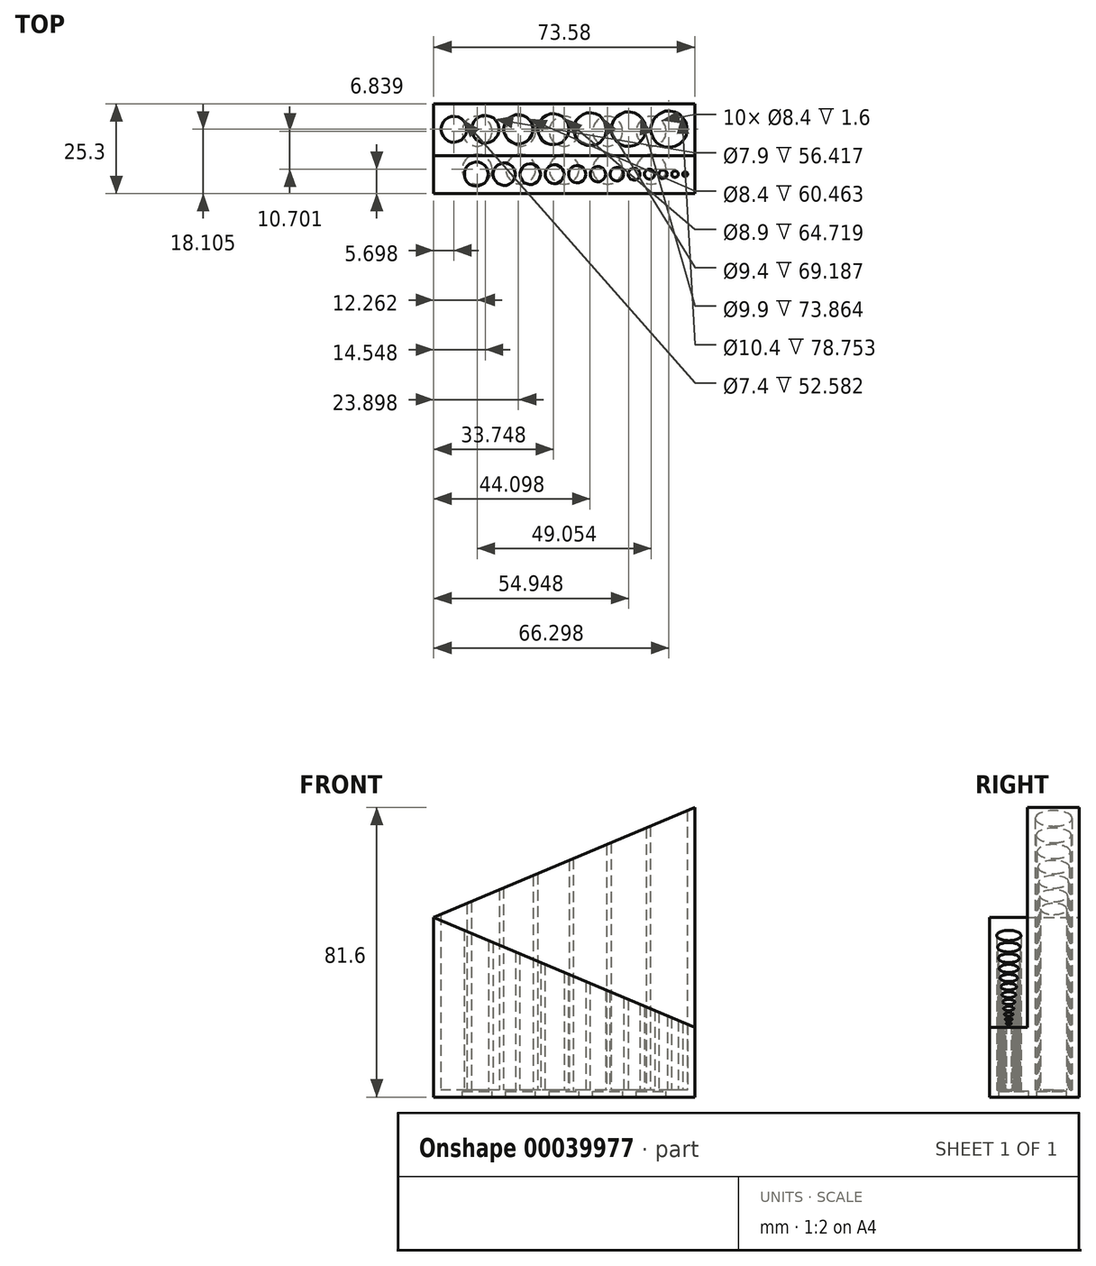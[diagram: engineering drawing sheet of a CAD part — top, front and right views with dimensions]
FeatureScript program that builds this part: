
annotation { "Feature Type Name" : "Feature", "Feature Type Description" : "" }
export const myFeature = defineFeature(function(context is Context, id is Id, definition is map)
    precondition{}
    {
        {
            var Q0;
            Q0=qCreatedBy(makeId("Top.planeOp"),FACE);
            var sketch = newSketch(context, id + "F0", { "sketchPlane" : qUnion([Q0])});
            skLineSegment(sketch, "E0.bottom", {"start": v(-27.23, 22.36) * mm, "end": v(46.35, 22.36) * mm});
            skLineSegment(sketch, "E0.top", {"start": v(-27.23, -2.94) * mm, "end": v(46.35, -2.94) * mm});
            skLineSegment(sketch, "E0.left", {"start": v(-27.23, 22.36) * mm, "end": v(-27.23, -2.94) * mm});
            skLineSegment(sketch, "E0.right", {"start": v(46.35, 22.36) * mm, "end": v(46.35, -2.94) * mm});
            skLineSegment(sketch, "E1", {"start": v(-27.23, 2.51) * mm, "end": v(46.35, 2.51) * mm, "construction": true});
            skCircle(sketch, "E2", {"center": v(43.65, 2.51) * mm, "radius": 0.7 * mm});
            skCircle(sketch, "E3", {"center": v(40.8, 2.51) * mm, "radius": 0.95 * mm});
            skCircle(sketch, "E4", {"center": v(37.45, 2.51) * mm, "radius": 1.2 * mm});
            skCircle(sketch, "E5", {"center": v(33.6, 2.51) * mm, "radius": 1.45 * mm});
            skCircle(sketch, "E6", {"center": v(29.25, 2.51) * mm, "radius": 1.7 * mm});
            skCircle(sketch, "E7", {"center": v(24.4, 2.51) * mm, "radius": 1.95 * mm});
            skCircle(sketch, "E8", {"center": v(19.05, 2.51) * mm, "radius": 2.2 * mm});
            skCircle(sketch, "E9", {"center": v(13.2, 2.51) * mm, "radius": 2.45 * mm});
            skLineSegment(sketch, "E10", {"start": v(-27.23, 15.16) * mm, "end": v(46.35, 15.16) * mm, "construction": true});
            skCircle(sketch, "E11", {"center": v(-12.68, 15.16) * mm, "radius": 3.95 * mm});
            skCircle(sketch, "E12", {"center": v(-3.33, 15.16) * mm, "radius": 4.2 * mm});
            skCircle(sketch, "E13", {"center": v(6.52, 15.16) * mm, "radius": 4.45 * mm});
            skCircle(sketch, "E14", {"center": v(16.87, 15.16) * mm, "radius": 4.7 * mm});
            skCircle(sketch, "E15", {"center": v(27.72, 15.16) * mm, "radius": 4.95 * mm});
            skCircle(sketch, "E16", {"center": v(39.07, 15.16) * mm, "radius": 5.2 * mm});
            skCircle(sketch, "E17", {"center": v(6.85, 2.51) * mm, "radius": 2.7 * mm});
            skCircle(sketch, "E18", {"center": v(0, 2.51) * mm, "radius": 2.95 * mm});
            skCircle(sketch, "E19", {"center": v(-7.35, 2.51) * mm, "radius": 3.2 * mm});
            skCircle(sketch, "E20", {"center": v(-21.53, 15.16) * mm, "radius": 3.7 * mm});
            skCircle(sketch, "E21", {"center": v(-15.2, 2.51) * mm, "radius": 3.45 * mm});
            skLineSegment(sketch, "E22", {"start": v(-27.23, 5.96) * mm, "end": v(46.35, 5.96) * mm, "construction": true});
            skLineSegment(sketch, "E23", {"start": v(-27.23, 9.96) * mm, "end": v(46.35, 9.96) * mm, "construction": true});
            skSolve(sketch);
        }
        {
            var Q0;
            Q0=makeQuery(id+"F0.imprint","IMPRINT",FACE,{"disambiguationData":[TD([[makeQuery(id+"F0.imprint","IMPRINT",EDGE,{"derivedFrom":sQuery(id+"F0.wireOp",EDGE,"E0.bottom")}),-1.0]])]});
            extrude(context, id + "F1", {"entities" : qUnion([Q0]), "depth" : 80 * mm});
        }
        {
            var Q0;
            Q0=makeQuery(id+"F1.opExtrude","SWEPT_FACE",FACE,{"disambiguationData":[OSD([sQuery(id+"F0.wireOp",EDGE,"E0.top")])]});
            var sketch = newSketch(context, id + "F2", { "sketchPlane" : qUnion([Q0])});
            skLineSegment(sketch, "E24", {"start": v(-27.23, 0) * mm, "end": v(46.35, 0) * mm});
            skLineSegment(sketch, "E25", {"start": v(46.35, 0) * mm, "end": v(46.35, 18) * mm});
            skLineSegment(sketch, "E26", {"start": v(46.35, 18) * mm, "end": v(-27.23, 49) * mm});
            skLineSegment(sketch, "E27", {"start": v(-27.23, 49) * mm, "end": v(-27.23, 0) * mm});
            skSolve(sketch);
        }
        {
            var Q0;
            Q0=makeQuery(id+"F0.imprint","IMPRINT",FACE,{"disambiguationData":[TD([[makeQuery(id+"F0.imprint","IMPRINT",EDGE,{"derivedFrom":sQuery(id+"F0.wireOp",EDGE,"E16")}),1.0]])]});
            var Q1;
            Q1=makeQuery(id+"F0.imprint","IMPRINT",FACE,{"disambiguationData":[TD([[makeQuery(id+"F0.imprint","IMPRINT",EDGE,{"derivedFrom":sQuery(id+"F0.wireOp",EDGE,"E15")}),1.0]])]});
            var Q2;
            Q2=makeQuery(id+"F0.imprint","IMPRINT",FACE,{"disambiguationData":[TD([[makeQuery(id+"F0.imprint","IMPRINT",EDGE,{"derivedFrom":sQuery(id+"F0.wireOp",EDGE,"E14")}),1.0]])]});
            var Q3;
            Q3=makeQuery(id+"F0.imprint","IMPRINT",FACE,{"disambiguationData":[TD([[makeQuery(id+"F0.imprint","IMPRINT",EDGE,{"derivedFrom":sQuery(id+"F0.wireOp",EDGE,"E13")}),1.0]])]});
            var Q4;
            Q4=makeQuery(id+"F0.imprint","IMPRINT",FACE,{"disambiguationData":[TD([[makeQuery(id+"F0.imprint","IMPRINT",EDGE,{"derivedFrom":sQuery(id+"F0.wireOp",EDGE,"E12")}),1.0]])]});
            var Q5;
            Q5=makeQuery(id+"F0.imprint","IMPRINT",FACE,{"disambiguationData":[TD([[makeQuery(id+"F0.imprint","IMPRINT",EDGE,{"derivedFrom":sQuery(id+"F0.wireOp",EDGE,"E11")}),1.0]])]});
            var Q6;
            Q6=makeQuery(id+"F0.imprint","IMPRINT",FACE,{"disambiguationData":[TD([[makeQuery(id+"F0.imprint","IMPRINT",EDGE,{"derivedFrom":sQuery(id+"F0.wireOp",EDGE,"E20")}),1.0]])]});
            var Q7;
            Q7=makeQuery(id+"F0.imprint","IMPRINT",FACE,{"disambiguationData":[TD([[makeQuery(id+"F0.imprint","IMPRINT",EDGE,{"derivedFrom":sQuery(id+"F0.wireOp",EDGE,"E19")}),1.0]])]});
            var Q8;
            Q8=makeQuery(id+"F0.imprint","IMPRINT",FACE,{"disambiguationData":[TD([[makeQuery(id+"F0.imprint","IMPRINT",EDGE,{"derivedFrom":sQuery(id+"F0.wireOp",EDGE,"E18")}),1.0]])]});
            var Q9;
            Q9=makeQuery(id+"F0.imprint","IMPRINT",FACE,{"disambiguationData":[TD([[makeQuery(id+"F0.imprint","IMPRINT",EDGE,{"derivedFrom":sQuery(id+"F0.wireOp",EDGE,"E17")}),1.0]])]});
            var Q10;
            Q10=makeQuery(id+"F0.imprint","IMPRINT",FACE,{"disambiguationData":[TD([[makeQuery(id+"F0.imprint","IMPRINT",EDGE,{"derivedFrom":sQuery(id+"F0.wireOp",EDGE,"E9")}),1.0]])]});
            var Q11;
            Q11=makeQuery(id+"F0.imprint","IMPRINT",FACE,{"disambiguationData":[TD([[makeQuery(id+"F0.imprint","IMPRINT",EDGE,{"derivedFrom":sQuery(id+"F0.wireOp",EDGE,"E8")}),1.0]])]});
            var Q12;
            Q12=makeQuery(id+"F0.imprint","IMPRINT",FACE,{"disambiguationData":[TD([[makeQuery(id+"F0.imprint","IMPRINT",EDGE,{"derivedFrom":sQuery(id+"F0.wireOp",EDGE,"E7")}),1.0]])]});
            var Q13;
            Q13=makeQuery(id+"F0.imprint","IMPRINT",FACE,{"disambiguationData":[TD([[makeQuery(id+"F0.imprint","IMPRINT",EDGE,{"derivedFrom":sQuery(id+"F0.wireOp",EDGE,"E21")}),1.0]])]});
            var Q14;
            Q14=makeQuery(id+"F0.imprint","IMPRINT",FACE,{"disambiguationData":[TD([[makeQuery(id+"F0.imprint","IMPRINT",EDGE,{"derivedFrom":sQuery(id+"F0.wireOp",EDGE,"E6")}),1.0]])]});
            var Q15;
            Q15=makeQuery(id+"F0.imprint","IMPRINT",FACE,{"disambiguationData":[TD([[makeQuery(id+"F0.imprint","IMPRINT",EDGE,{"derivedFrom":sQuery(id+"F0.wireOp",EDGE,"E5")}),1.0]])]});
            var Q16;
            Q16=makeQuery(id+"F0.imprint","IMPRINT",FACE,{"disambiguationData":[TD([[makeQuery(id+"F0.imprint","IMPRINT",EDGE,{"derivedFrom":sQuery(id+"F0.wireOp",EDGE,"E4")}),1.0]])]});
            var Q17;
            Q17=makeQuery(id+"F0.imprint","IMPRINT",FACE,{"disambiguationData":[TD([[makeQuery(id+"F0.imprint","IMPRINT",EDGE,{"derivedFrom":sQuery(id+"F0.wireOp",EDGE,"E3")}),1.0]])]});
            var Q18;
            Q18=makeQuery(id+"F0.imprint","IMPRINT",FACE,{"disambiguationData":[TD([[makeQuery(id+"F0.imprint","IMPRINT",EDGE,{"derivedFrom":sQuery(id+"F0.wireOp",EDGE,"E0.bottom")}),-1.0]])]});
            var Q19;
            Q19=makeQuery(id+"F0.imprint","IMPRINT",FACE,{"disambiguationData":[TD([[makeQuery(id+"F0.imprint","IMPRINT",EDGE,{"derivedFrom":sQuery(id+"F0.wireOp",EDGE,"E2")}),1.0]])]});
            extrude(context, id + "F3", {"entities" : qUnion([Q0, Q1, Q2, Q3, Q4, Q5, Q6, Q7, Q8, Q9, Q10, Q11, Q12, Q13, Q14, Q15, Q16, Q17, Q18, Q19]), "depth" : 0.4 * mm});
        }
        {
            var Q0;
            {var subQ3=sQuery(id+"F2.wireOp",EDGE,"E26");Q0=makeQuery(id+"F2.imprint","IMPRINT",FACE,{"disambiguationData":[TD([[makeQuery(id+"F2.imprint","IMPRINT",EDGE,{"derivedFrom":subQ3}),-1.0]])]});}
            extrude(context, id + "F4", {"entities" : qUnion([Q0]), "operationType" : NewBodyOperationType.REMOVE, "oppositeDirection" : true, "depth" : 10.7 * mm});
        }
        {
            var Q0;
            Q0=makeQuery(id+"F1.opExtrude","SWEPT_FACE",FACE,{"disambiguationData":[OSD([sQuery(id+"F0.wireOp",EDGE,"E0.bottom")])]});
            var sketch = newSketch(context, id + "F5", { "sketchPlane" : qUnion([Q0])});
            skLineSegment(sketch, "E28", {"start": v(27.23, 0) * mm, "end": v(-46.35, 0) * mm});
            skLineSegment(sketch, "E29", {"start": v(-46.35, 0) * mm, "end": v(-46.35, 80) * mm});
            skLineSegment(sketch, "E30", {"start": v(-46.35, 80) * mm, "end": v(27.23, 49) * mm});
            skLineSegment(sketch, "E31", {"start": v(27.23, 49) * mm, "end": v(27.23, 0) * mm});
            skSolve(sketch);
        }
        {
            var Q0;
            {var subQ3=sQuery(id+"F5.wireOp",EDGE,"E30");Q0=makeQuery(id+"F5.imprint","IMPRINT",FACE,{"disambiguationData":[TD([[makeQuery(id+"F5.imprint","IMPRINT",EDGE,{"derivedFrom":subQ3}),1.0]])]});}
            extrude(context, id + "F6", {"entities" : qUnion([Q0]), "operationType" : NewBodyOperationType.REMOVE, "oppositeDirection" : true, "depth" : 25 * mm});
        }
        {
            var Q0;
            Q0=makeQuery(id+"F3.opExtrude","CAP_FACE",FACE,{"disambiguationData":[OSD([sQuery(id+"F0.wireOp",EDGE,"E0.bottom"),sQuery(id+"F0.wireOp",EDGE,"E0.top"),sQuery(id+"F0.wireOp",EDGE,"E0.left"),sQuery(id+"F0.wireOp",EDGE,"E0.right")])],"isStart":true});
            var sketch = newSketch(context, id + "F7", { "sketchPlane" : qUnion([Q0])});
            skLineSegment(sketch, "E32.bottom", {"start": v(-27.23, 2.94) * mm, "end": v(46.35, 2.94) * mm});
            skLineSegment(sketch, "E32.top", {"start": v(-27.23, -22.36) * mm, "end": v(46.35, -22.36) * mm});
            skLineSegment(sketch, "E32.left", {"start": v(-27.23, 2.94) * mm, "end": v(-27.23, -22.36) * mm});
            skLineSegment(sketch, "E32.right", {"start": v(46.35, 2.94) * mm, "end": v(46.35, -22.36) * mm});
            skCircle(sketch, "E33", {"center": v(-14.97, -3.9) * mm, "radius": 4.2 * mm});
            skCircle(sketch, "E34", {"center": v(-2.7, -3.9) * mm, "radius": 4.2 * mm});
            skCircle(sketch, "E35", {"center": v(9.56, -3.9) * mm, "radius": 4.2 * mm});
            skCircle(sketch, "E36", {"center": v(21.82, -3.9) * mm, "radius": 4.2 * mm});
            skCircle(sketch, "E37", {"center": v(34.09, -14.6) * mm, "radius": 4.2 * mm});
            skCircle(sketch, "E38", {"center": v(21.82, -14.6) * mm, "radius": 4.2 * mm});
            skCircle(sketch, "E39", {"center": v(9.56, -14.6) * mm, "radius": 4.2 * mm});
            skCircle(sketch, "E40", {"center": v(-2.7, -14.6) * mm, "radius": 4.2 * mm});
            skLineSegment(sketch, "E41", {"start": v(-14.97, -3.9) * mm, "end": v(-27.23, -3.9) * mm});
            skLineSegment(sketch, "E42", {"start": v(-14.97, -3.9) * mm, "end": v(-2.7, -3.9) * mm});
            skLineSegment(sketch, "E43", {"start": v(-2.7, -3.9) * mm, "end": v(9.56, -3.9) * mm});
            skLineSegment(sketch, "E44", {"start": v(9.56, -3.9) * mm, "end": v(21.82, -3.9) * mm});
            skLineSegment(sketch, "E45", {"start": v(21.82, -3.9) * mm, "end": v(34.09, -3.9) * mm});
            skLineSegment(sketch, "E46", {"start": v(34.09, -3.9) * mm, "end": v(46.35, -3.9) * mm});
            skLineSegment(sketch, "E47", {"start": v(34.09, -14.6) * mm, "end": v(46.35, -14.6) * mm});
            skLineSegment(sketch, "E48", {"start": v(34.09, -14.6) * mm, "end": v(21.82, -14.6) * mm});
            skLineSegment(sketch, "E49", {"start": v(21.82, -14.6) * mm, "end": v(9.56, -14.6) * mm});
            skLineSegment(sketch, "E50", {"start": v(9.56, -14.6) * mm, "end": v(-2.7, -14.6) * mm});
            skLineSegment(sketch, "E51", {"start": v(-2.7, -14.6) * mm, "end": v(-14.97, -14.6) * mm});
            skLineSegment(sketch, "E52", {"start": v(-14.97, -14.6) * mm, "end": v(-27.23, -14.6) * mm});
            skCircle(sketch, "E53", {"center": v(-14.97, -14.6) * mm, "radius": 4.2 * mm});
            skCircle(sketch, "E54", {"center": v(34.09, -3.9) * mm, "radius": 4.2 * mm});
            skSolve(sketch);
        }
        {
            var Q0;
            {var subQ27=sQuery(id+"F7.wireOp",EDGE,"E32.left");var subQ32=sQuery(id+"F7.wireOp",EDGE,"E41");var subQ38=makeQuery(id+"F7.imprint","INTERSECT",VERTEX,{"derivedFrom":[subQ27,subQ32]});Q0=makeQuery(id+"F7.imprint","IMPRINT",FACE,{"disambiguationData":[TD([[makeQuery(id+"F7.imprint","IMPRINT",EDGE,{"disambiguationData":[TD([[subQ38,1.0]])],"derivedFrom":subQ27}),-1.0]])]});}
            var Q1;
            {var subQ12=sQuery(id+"F7.wireOp",EDGE,"E32.bottom");Q1=makeQuery(id+"F7.imprint","IMPRINT",FACE,{"disambiguationData":[TD([[makeQuery(id+"F7.imprint","IMPRINT",EDGE,{"derivedFrom":subQ12}),-1.0]])]});}
            var Q2;
            {var subQ10=sQuery(id+"F7.wireOp",EDGE,"E32.top");Q2=makeQuery(id+"F7.imprint","IMPRINT",FACE,{"disambiguationData":[TD([[makeQuery(id+"F7.imprint","IMPRINT",EDGE,{"derivedFrom":subQ10}),1.0]])]});}
            extrude(context, id + "F8", {"entities" : qUnion([Q0, Q1, Q2]), "operationType" : NewBodyOperationType.ADD, "depth" : 1.6 * mm});
        }
    });
